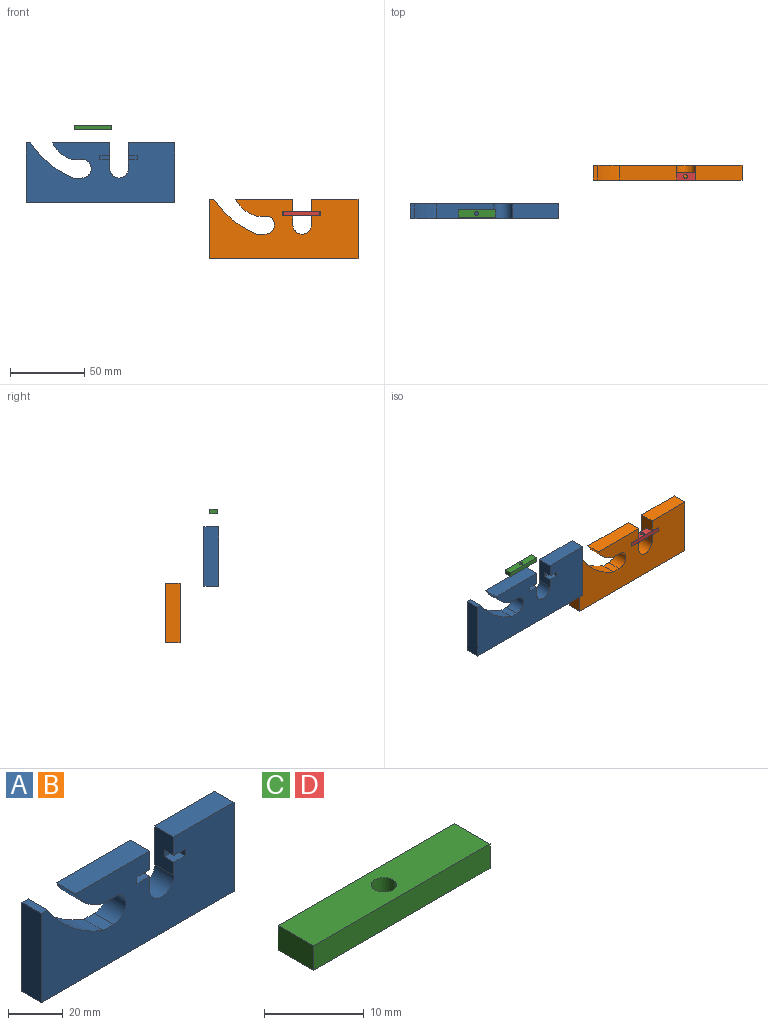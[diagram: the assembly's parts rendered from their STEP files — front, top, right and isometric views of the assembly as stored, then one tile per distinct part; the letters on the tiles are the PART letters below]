
ASSEMBLY  parts=4 mates=1
PART A: 24 faces, bbox 100x10x40 mm
  f0: plane 17.28x10mm, normal (-1,0,0), area 157.8mm2, adj f1,f9,f10,f15,f16,f17,f19
  f1: plane 100x40mm, normal (0,-1,0), area 3246.8mm2, adj f0,f2,f3,f4,f5,f6,f7,f8
  f2: cylinder r=6.31mm len=12.16mm, axis (0,1,0), area 173.8mm2, adj f1,f3,f14,f15
  f3: plane 10x5.43mm, normal (0,0,1), area 54.3mm2, adj f1,f2,f4,f15
  f4: cylinder r=59.49mm len=28.82mm, axis (0,1,0), area 378.9mm2, adj f1,f3,f5,f15
  f5: plane 10x3.25mm, normal (0,0,1), area 32.5mm2, adj f1,f4,f6,f15
  f6: plane 40x10mm, normal (-1,0,0), area 400mm2, adj f1,f5,f7,f15
  f7: plane 100x10mm, normal (0,0,-1), area 1000mm2, adj f1,f6,f8,f15
  f8: plane 40x10mm, normal (1,0,0), area 400mm2, adj f1,f7,f9,f15
  f9: plane 31.19x10mm, normal (0,0,1), area 311.9mm2, adj f0,f1,f8,f15
  f10: cylinder r=6.31mm len=12.63mm, axis (0,1,0), area 198.3mm2, adj f0,f1,f11,f15
  f11: plane 17.28x10mm, normal (1,0,0), area 157.8mm2, adj f1,f10,f12,f15,f20,f22,f23
  f12: plane 38.47x10mm, normal (0,0,1), area 384.7mm2, adj f1,f11,f13,f15
  f13: cylinder r=21.8mm len=14.36mm, axis (0,1,0), area 189.5mm2, adj f1,f12,f14,f15
  f14: plane 10x7.82mm, normal (0,0,-1), area 78.2mm2, adj f1,f2,f13,f15
  f15: plane 100x40mm, normal (0,1,0), area 3283.9mm2, adj f0,f2,f3,f4,f5,f6,f7,f8
  f16: plane 5.83x5mm, normal (0,0,-1), area 29.1mm2, adj f0,f1,f18,f19
  f17: plane 5.83x5mm, normal (0,0,1), area 29.1mm2, adj f0,f1,f18,f19
  f18: plane 5x3mm, normal (-1,0,0), area 15mm2, adj f1,f16,f17,f19
  f19: plane 5.83x3mm, normal (0,-1,0), area 17.5mm2, adj f0,f16,f17,f18
  f20: plane 6.55x5mm, normal (0,0,-1), area 32.7mm2, adj f1,f11,f21,f23
  f21: plane 5x3mm, normal (1,0,0), area 15mm2, adj f1,f20,f22,f23
  f22: plane 6.55x5mm, normal (0,0,1), area 32.7mm2, adj f1,f11,f21,f23
  f23: plane 6.55x3mm, normal (0,-1,0), area 19.6mm2, adj f11,f20,f21,f22
PART B: same geometry as A
PART C: 7 faces, bbox 25x5x3 mm
  f0: plane 25x5mm, normal (0,0,1), area 120.1mm2, adj f1,f3,f4,f5,f6
  f1: plane 5x3mm, normal (-1,0,0), area 15mm2, adj f0,f2,f4,f5
  f2: plane 25x5mm, normal (0,0,-1), area 120.1mm2, adj f1,f3,f4,f5,f6
  f3: plane 5x3mm, normal (1,0,0), area 15mm2, adj f0,f2,f4,f5
  f4: plane 25x3mm, normal (0,-1,0), area 75mm2, adj f0,f1,f2,f3
  f5: plane 25x3mm, normal (0,1,0), area 75mm2, adj f0,f1,f2,f3
  f6: cylinder r=1.25mm len=3mm, axis (0,0,1), area 23.6mm2, adj f0,f2
PART D: same geometry as C
PLACE A t=(-70.2,-7.82,-6.81)mm
PLACE B t=(52.77,18.15,-44.48)mm
PLACE C t=(-87.39,-1.87,56.98)mm
PLACE D t=(52.69,23.15,-0.74)mm
MATE fastened B.f23 <-> D.f5  axis (0,-1,0) through (59.16,13.15,-23.27)mm
